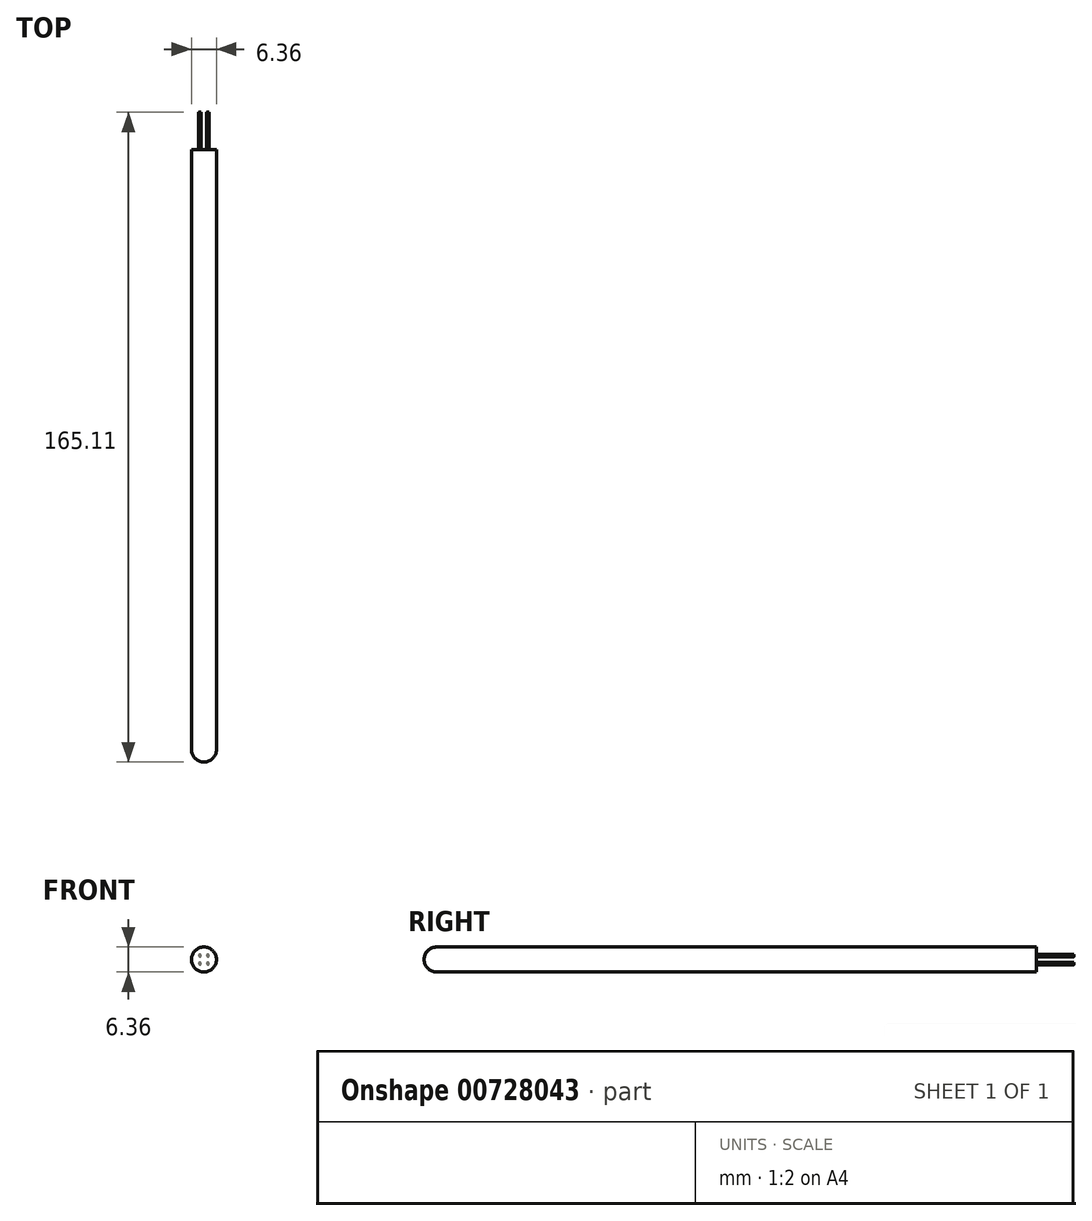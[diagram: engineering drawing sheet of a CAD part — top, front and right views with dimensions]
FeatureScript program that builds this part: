
annotation { "Feature Type Name" : "Feature", "Feature Type Description" : "" }
export const myFeature = defineFeature(function(context is Context, id is Id, definition is map)
    precondition{}
    {
        {
            var Q0;
            Q0=qCreatedBy(makeId("Front.planeOp"),FACE);
            var sketch = newSketch(context, id + "F0", { "sketchPlane" : qUnion([Q0])});
            skCircle(sketch, "E0", {"center": v(0, 0) * mm, "radius": 3.18 * mm});
            skSolve(sketch);
        }
        {
            var Q0;
            Q0=makeQuery(id+"F0.imprint","IMPRINT",FACE,{"disambiguationData":[TD([[makeQuery(id+"F0.imprint","IMPRINT",EDGE,{"derivedFrom":sQuery(id+"F0.wireOp",EDGE,"E0")}),1.0]])]});
            extrude(context, id + "F1", {"entities" : qUnion([Q0]), "depth" : 152.4 * mm, "offsetDistance" : 25.4 * mm});
        }
        {
            var Q0;
            Q0=qCreatedBy(makeId("Right.planeOp"),FACE);
            var sketch = newSketch(context, id + "F2", { "sketchPlane" : qUnion([Q0])});
            skLineSegment(sketch, "E1", {"start": v(-152.4, 0) * mm, "end": v(-185.55, 0) * mm, "construction": true});
            skArc(sketch, "E2", {"start": v(-152.4, 3.18) * mm, "mid": v(-154.65, 2.25) * mm, "end": v(-155.58, 0) * mm});
            skLineSegment(sketch, "E3", {"start": v(-152.4, 3.18) * mm, "end": v(-152.4, 0) * mm});
            skLineSegment(sketch, "E4", {"start": v(-152.4, 0) * mm, "end": v(-155.58, 0) * mm});
            skSolve(sketch);
        }
        {
            var Q0;
            Q0=makeQuery(id+"F2.imprint","IMPRINT",FACE,{"disambiguationData":[TD([[makeQuery(id+"F2.imprint","IMPRINT",EDGE,{"derivedFrom":sQuery(id+"F2.wireOp",EDGE,"E2")}),1.0]])]});
            var Q1;
            Q1=sQuery(id+"F2.wireOp",EDGE,"E1");
            revolve(context, id + "F3", {"operationType" : NewBodyOperationType.ADD, "surfaceOperationType" : NewSurfaceOperationType.NEW, "entities" : qUnion([Q0]), "axis" : qUnion([Q1]), "revolveType" : RevolveType.FULL});
        }
        {
            var Q0;
            Q0=makeQuery(id+"F1.opExtrude","CAP_FACE",FACE,{"disambiguationData":[OSD([sQuery(id+"F0.wireOp",EDGE,"E0")])],"isStart":true});
            var sketch = newSketch(context, id + "F4", { "sketchPlane" : qUnion([Q0])});
            skCircle(sketch, "E5", {"center": v(1.02, -1.02) * mm, "radius": 0.32 * mm});
            skCircle(sketch, "E6.0.1.0", {"center": v(1.02, 1.02) * mm, "radius": 0.32 * mm});
            skCircle(sketch, "E6.1.0.0", {"center": v(-1.02, -1.02) * mm, "radius": 0.32 * mm});
            skCircle(sketch, "E6.1.1.0", {"center": v(-1.02, 1.02) * mm, "radius": 0.32 * mm});
            skLineSegment(sketch, "E6.direction1", {"start": v(1.02, -1.02) * mm, "end": v(-1.02, -1.02) * mm, "construction": true});
            skLineSegment(sketch, "E6.direction2", {"start": v(1.02, -1.02) * mm, "end": v(1.02, 1.02) * mm, "construction": true});
            skSolve(sketch);
        }
        {
            var Q0;
            Q0=makeQuery(id+"F4.imprint","IMPRINT",FACE,{"disambiguationData":[TD([[makeQuery(id+"F4.imprint","IMPRINT",EDGE,{"derivedFrom":sQuery(id+"F4.wireOp",EDGE,"E5")}),1.0]])]});
            var Q1;
            Q1=makeQuery(id+"F4.imprint","IMPRINT",FACE,{"disambiguationData":[TD([[makeQuery(id+"F4.imprint","IMPRINT",EDGE,{"derivedFrom":sQuery(id+"F4.wireOp",EDGE,"E6.1.0.0")}),1.0]])]});
            var Q2;
            Q2=makeQuery(id+"F4.imprint","IMPRINT",FACE,{"disambiguationData":[TD([[makeQuery(id+"F4.imprint","IMPRINT",EDGE,{"derivedFrom":sQuery(id+"F4.wireOp",EDGE,"E6.0.1.0")}),1.0]])]});
            var Q3;
            Q3=makeQuery(id+"F4.imprint","IMPRINT",FACE,{"disambiguationData":[TD([[makeQuery(id+"F4.imprint","IMPRINT",EDGE,{"derivedFrom":sQuery(id+"F4.wireOp",EDGE,"E6.1.1.0")}),1.0]])]});
            extrude(context, id + "F5", {"entities" : qUnion([Q0, Q1, Q2, Q3]), "operationType" : NewBodyOperationType.ADD, "depth" : 9.52 * mm, "offsetDistance" : 25.4 * mm});
        }
    });
